# Revit family: Facade_60_Curtain_Wall_S12_Standard
name_source: partatom
category: Windows
revit_build: Autodesk Revit 2014 (Build: 20130308_1515(x64)
units: mm (PartAtom-declared; Revit-internal decimal feet)

## types (48) — shared parameters
100mm Mullion = Yes
160mm Mullion = No
190mm Mullion = No
Custom Offset From Exterior = 10 mm  [stored 0.0328084 ft]
DG Gasket Thickness = 12 mm  [stored 0.0393701 ft]
Description = Curtain wall, S12
Frame Bottom Gap = 30 mm  [stored 0.0984252 ft]
Frame Thickness = 102 mm
Glazing Bottom Gap = 70 mm
Glazing Side Gap = 40 mm  [stored 0.131234 ft]
Glazing Top Gap = 40 mm  [stored 0.131234 ft]
Half Expansion Break = No
Jamb Width = 60 mm  [stored 0.19685 ft]
Limit Door Height Max = 12129 mm
Limit Door Height Min = 729 mm
Limit Door Width Max = 3080 mm
Limit Door Width Min = 380 mm
Limit Panel Height Max = 6000 mm  [stored 19.685 ft]
Limit Panel Height Min = 300 mm
Limit Panel Width Max = 3000 mm  [stored 9.84252 ft]
Limit Panel Width Min = 300 mm
Manufacturer = Crealco
Max System DG Unit Thickness = 25 mm  [stored 0.082021 ft]
Model = Façade 60
Mullion Configuration = 1 mm  [stored 0.00328084 ft]
Quarter Expansion Break = No
Sill Height = 85 mm  [stored 0.278871 ft]
Thermal Break Material = Plastic, Opaque Black
URL = http://www.crealco.co.za
Wall Closure = By host
zero-valued in all types: Default Sill Height

## per-type parameters (varying)
| type | Custom Curtain Wall Height | Custom Curtain Wall Width | Custom Windload | Intruderprufe Insulated LowE SHGC Value | Intruderprufe Insulated LowE U Value | Intruderprufe Insulated SHGC Value | Intruderprufe Insulated U Value | Intruderprufe LowE SHGC Value | Intruderprufe LowE U Value | Intruderprufe SHGC Value | Intruderprufe U Value |
| F60-S12-0925-1000Pa | 2490 mm | 890 mm  [stored 2.91995 ft] | 1000 mm  [stored 3.28084 ft] | 0.503 | 2.7 | 0.558 | 3.27 | 0.567 | 4.51 | 0.646 | 5.75 |
| F60-S12-0925-1500Pa | 2490 mm | 890 mm  [stored 2.91995 ft] | 1500 mm  [stored 4.92126 ft] | 0.503 | 2.7 | 0.558 | 3.27 | 0.567 | 4.51 | 0.646 | 5.75 |
| F60-S12-0925-2000Pa | 2490 mm | 890 mm  [stored 2.91995 ft] | 2000 mm  [stored 6.56168 ft] | 0.503 | 2.7 | 0.558 | 3.27 | 0.567 | 4.51 | 0.646 | 5.75 |
| F60-S12-1225-1000Pa | 2490 mm | 1190 mm  [stored 3.9042 ft] | 1000 mm  [stored 3.28084 ft] | 0.521 | 2.58 | 0.578 | 3.19 | 0.587 | 4.4 | 0.67 | 5.76 |
| F60-S12-1225-1500Pa | 2490 mm | 1190 mm  [stored 3.9042 ft] | 1500 mm  [stored 4.92126 ft] | 0.521 | 2.58 | 0.578 | 3.19 | 0.587 | 4.4 | 0.67 | 5.76 |
| F60-S12-1225-2000Pa | 2490 mm | 1190 mm  [stored 3.9042 ft] | 2000 mm  [stored 6.56168 ft] | 0.521 | 2.58 | 0.578 | 3.19 | 0.587 | 4.4 | 0.67 | 5.76 |
| F60-S12-1525-1000Pa | 2490 mm | 1490 mm  [stored 4.88845 ft] | 1000 mm  [stored 3.28084 ft] | 0.532 | 2.51 | 0.59 | 3.14 | 0.6 | 4.33 | 0.684 | 5.76 |
| F60-S12-1525-1500Pa | 2490 mm | 1490 mm  [stored 4.88845 ft] | 1500 mm  [stored 4.92126 ft] | 0.532 | 2.51 | 0.59 | 3.14 | 0.6 | 4.33 | 0.684 | 5.76 |
| F60-S12-1525-2000Pa | 2490 mm | 1490 mm  [stored 4.88845 ft] | 2000 mm  [stored 6.56168 ft] | 0.532 | 2.51 | 0.59 | 3.14 | 0.6 | 4.33 | 0.684 | 5.76 |
| F60-S12-1825-1000Pa | 2490 mm | 1790 mm  [stored 5.8727 ft] | 1000 mm  [stored 3.28084 ft] | 0.539 | 2.47 | 0.598 | 3.11 | 0.608 | 4.28 | 0.694 | 5.77 |
| F60-S12-1825-1500Pa | 2490 mm | 1790 mm  [stored 5.8727 ft] | 1500 mm  [stored 4.92126 ft] | 0.539 | 2.47 | 0.598 | 3.11 | 0.608 | 4.28 | 0.694 | 5.77 |
| F60-S12-1825-2000Pa | 2490 mm | 1790 mm  [stored 5.8727 ft] | 2000 mm  [stored 6.56168 ft] | 0.539 | 2.47 | 0.598 | 3.11 | 0.608 | 4.28 | 0.694 | 5.77 |
| F60-S12-2125-1000Pa | 2490 mm | 2090 mm  [stored 6.85696 ft] | 1000 mm  [stored 3.28084 ft] | 0.544 | 2.44 | 0.603 | 3.08 | 0.614 | 4.25 | 0.7 | 5.77 |
| F60-S12-2125-1500Pa | 2490 mm | 2090 mm  [stored 6.85696 ft] | 1500 mm  [stored 4.92126 ft] | 0.544 | 2.44 | 0.603 | 3.08 | 0.614 | 4.25 | 0.7 | 5.77 |
| F60-S12-2125-2000Pa | 2490 mm | 2090 mm  [stored 6.85696 ft] | 2000 mm  [stored 6.56168 ft] | 0.544 | 2.44 | 0.603 | 3.08 | 0.614 | 4.25 | 0.7 | 5.77 |
| F60-S12-2425-1000Pa | 2490 mm | 2390 mm  [stored 7.84121 ft] | 1000 mm  [stored 3.28084 ft] | 0.547 | 2.41 | 0.607 | 3.07 | 0.618 | 4.23 | 0.706 | 5.77 |
| F60-S12-2425-1500Pa | 2490 mm | 2390 mm  [stored 7.84121 ft] | 1500 mm  [stored 4.92126 ft] | 0.547 | 2.41 | 0.607 | 3.07 | 0.618 | 4.23 | 0.706 | 5.77 |
| F60-S12-2425-2000Pa | 2490 mm | 2390 mm  [stored 7.84121 ft] | 2000 mm  [stored 6.56168 ft] | 0.547 | 2.41 | 0.607 | 3.07 | 0.618 | 4.23 | 0.706 | 5.77 |
| F60-S12-2725-1000Pa | 2490 mm | 2690 mm | 1000 mm  [stored 3.28084 ft] | 0.547 | 2.41 | 0.607 | 3.07 | 0.618 | 4.23 | 0.7063 | 5.77 |
| F60-S12-2725-1500Pa | 2490 mm | 2690 mm | 1500 mm  [stored 4.92126 ft] | 0.547 | 2.41 | 0.607 | 3.07 | 0.618 | 4.23 | 0.7063 | 5.77 |
| F60-S12-2725-2000Pa | 2490 mm | 2690 mm | 2000 mm  [stored 6.56168 ft] | 0.547 | 2.41 | 0.607 | 3.07 | 0.618 | 4.23 | 0.7063 | 5.77 |
| F60-S12-3025-1000Pa | 2490 mm | 2990 mm  [stored 9.80971 ft] | 1000 mm  [stored 3.28084 ft] | 0.553 | 2.38 | 0.613 | 3.04 | 0.624 | 4.2 | 0.713 | 5.77 |
| F60-S12-3025-1500Pa | 2490 mm | 2990 mm  [stored 9.80971 ft] | 1500 mm  [stored 4.92126 ft] | 0.553 | 2.38 | 0.613 | 3.04 | 0.624 | 4.2 | 0.713 | 5.77 |
| F60-S12-3025-2000Pa | 2490 mm | 2990 mm  [stored 9.80971 ft] | 2000 mm  [stored 6.56168 ft] | 0.553 | 2.38 | 0.613 | 3.04 | 0.624 | 4.2 | 0.713 | 5.77 |
| F60-S12-0950-1000Pa | 4990 mm  [stored 16.3714 ft] | 890 mm  [stored 2.91995 ft] | 1000 mm  [stored 3.28084 ft] | 0.524 | 2.55 | 0.581 | 3.16 | 0.591 | 4.35 | 0.674 | 5.73 |
| F60-S12-0950-1500Pa | 4990 mm  [stored 16.3714 ft] | 890 mm  [stored 2.91995 ft] | 1500 mm  [stored 4.92126 ft] | 0.524 | 2.55 | 0.581 | 3.16 | 0.591 | 4.35 | 0.674 | 5.73 |
| F60-S12-0950-2000Pa | 4990 mm  [stored 16.3714 ft] | 890 mm  [stored 2.91995 ft] | 2000 mm  [stored 6.56168 ft] | 0.524 | 2.55 | 0.581 | 3.16 | 0.591 | 4.35 | 0.674 | 5.73 |
| F60-S12-1250-1000Pa | 4990 mm  [stored 16.3714 ft] | 1190 mm  [stored 3.9042 ft] | 1000 mm  [stored 3.28084 ft] | 0.543 | 2.42 | 0.602 | 3.07 | 0.613 | 4.22 | 0.699 | 5.74 |
| F60-S12-1250-1500Pa | 4990 mm  [stored 16.3714 ft] | 1190 mm  [stored 3.9042 ft] | 1500 mm  [stored 4.92126 ft] | 0.543 | 2.42 | 0.602 | 3.07 | 0.613 | 4.22 | 0.699 | 5.74 |
| F60-S12-1250-2000Pa | 4990 mm  [stored 16.3714 ft] | 1190 mm  [stored 3.9042 ft] | 2000 mm  [stored 6.56168 ft] | 0.543 | 2.42 | 0.602 | 3.07 | 0.613 | 4.22 | 0.699 | 5.74 |
| F60-S12-1550-1000Pa | 4990 mm  [stored 16.3714 ft] | 1490 mm  [stored 4.88845 ft] | 1000 mm  [stored 3.28084 ft] | 0.554 | 2.35 | 0.615 | 6.02 | 0.626 | 4.14 | 0.714 | 5.74 |
| F60-S12-1550-1500Pa | 4990 mm  [stored 16.3714 ft] | 1490 mm  [stored 4.88845 ft] | 1500 mm  [stored 4.92126 ft] | 0.554 | 2.35 | 0.615 | 6.02 | 0.626 | 4.14 | 0.714 | 5.74 |
| F60-S12-1550-2000Pa | 4990 mm  [stored 16.3714 ft] | 1490 mm  [stored 4.88845 ft] | 2000 mm  [stored 6.56168 ft] | 0.554 | 2.35 | 0.615 | 6.02 | 0.626 | 4.14 | 0.714 | 5.74 |
| F60-S12-1850-1000Pa | 4990 mm  [stored 16.3714 ft] | 1790 mm  [stored 5.8727 ft] | 1000 mm  [stored 3.28084 ft] | 0.561 | 2.3 | 0.623 | 2.98 | 0.634 | 4.09 | 0.724 | 5.758 |
| F60-S12-1850-1500Pa | 4990 mm  [stored 16.3714 ft] | 1790 mm  [stored 5.8727 ft] | 1500 mm  [stored 4.92126 ft] | 0.561 | 2.3 | 0.623 | 2.98 | 0.634 | 4.09 | 0.724 | 5.758 |
| F60-S12-1850-2000Pa | 4990 mm  [stored 16.3714 ft] | 1790 mm  [stored 5.8727 ft] | 2000 mm  [stored 6.56168 ft] | 0.561 | 2.3 | 0.623 | 2.98 | 0.634 | 4.09 | 0.724 | 5.758 |
| F60-S12-2150-1000Pa | 4990 mm  [stored 16.3714 ft] | 2090 mm  [stored 6.85696 ft] | 1000 mm  [stored 3.28084 ft] | 0.567 | 2.27 | 0.629 | 2.96 | 0.64 | 4.06 | 0.731 | 5.75 |
| F60-S12-2150-1500Pa | 4990 mm  [stored 16.3714 ft] | 2090 mm  [stored 6.85696 ft] | 1500 mm  [stored 4.92126 ft] | 0.567 | 2.27 | 0.629 | 2.96 | 0.64 | 4.06 | 0.731 | 5.75 |
| F60-S12-2150-2000Pa | 4990 mm  [stored 16.3714 ft] | 2090 mm  [stored 6.85696 ft] | 2000 mm  [stored 6.56168 ft] | 0.567 | 2.27 | 0.629 | 2.96 | 0.64 | 4.06 | 0.731 | 5.75 |
| F60-S12-2450-1000Pa | 4990 mm  [stored 16.3714 ft] | 2390 mm  [stored 7.84121 ft] | 1000 mm  [stored 3.28084 ft] | 0.57 | 2.24 | 0.633 | 2.94 | 0.645 | 4.03 | 0.737 | 5.75 |
| F60-S12-2450-1500Pa | 4990 mm  [stored 16.3714 ft] | 2390 mm  [stored 7.84121 ft] | 1500 mm  [stored 4.92126 ft] | 0.57 | 2.24 | 0.633 | 2.94 | 0.645 | 4.03 | 0.737 | 5.75 |
| F60-S12-2450-2000Pa | 4990 mm  [stored 16.3714 ft] | 2390 mm  [stored 7.84121 ft] | 2000 mm  [stored 6.56168 ft] | 0.57 | 2.24 | 0.633 | 2.94 | 0.645 | 4.03 | 0.737 | 5.75 |
| F60-S12-2750-1000Pa | 4990 mm  [stored 16.3714 ft] | 2690 mm | 1000 mm  [stored 3.28084 ft] | 0.57 | 2.24 | 0.633 | 2.94 | 0.645 | 4.03 | 0.737 | 5.75 |
| F60-S12-2750-1500Pa | 4990 mm  [stored 16.3714 ft] | 2690 mm | 1500 mm  [stored 4.92126 ft] | 0.57 | 2.24 | 0.633 | 2.94 | 0.645 | 4.03 | 0.737 | 5.75 |
| F60-S12-2750-2000Pa | 4990 mm  [stored 16.3714 ft] | 2690 mm | 2000 mm  [stored 6.56168 ft] | 0.57 | 2.24 | 0.633 | 2.94 | 0.645 | 4.03 | 0.737 | 5.75 |
| F60-S12-3050-1000Pa | 4990 mm  [stored 16.3714 ft] | 2990 mm  [stored 9.80971 ft] | 1000 mm  [stored 3.28084 ft] | 0.576 | 0.22 | 0.639 | 2.91 | 0.651 | 3.99 | 0.744 | 5.76 |
| F60-S12-3050-1500Pa | 4990 mm  [stored 16.3714 ft] | 2990 mm  [stored 9.80971 ft] | 1000 mm  [stored 3.28084 ft] | 0.576 | 0.22 | 0.639 | 2.91 | 0.651 | 3.99 | 0.744 | 5.76 |
| F60-S12-3050-2000Pa | 4990 mm  [stored 16.3714 ft] | 2990 mm  [stored 9.80971 ft] | 1000 mm  [stored 3.28084 ft] | 0.576 | 0.22 | 0.639 | 2.91 | 0.651 | 3.99 | 0.744 | 5.76 |

note: [stored X ft] marks values corroborated as IEEE doubles in the binary element streams (Revit-internal decimal feet)

## geometry (parser evidence)
native form markers: Sweep x17
no freeform markers — native parametric forms only
